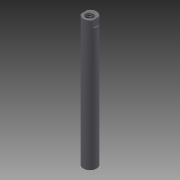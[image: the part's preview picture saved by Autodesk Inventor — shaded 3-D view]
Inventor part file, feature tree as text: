
AUTODESK INVENTOR PART (.ipt)
format: ipt  version: 2014 (Build 180170000, 170)  size: 134,656 bytes
history: native  units: in
note: dims shown in document units (in); Inventor stores cm internally (conversion verified against a paired STEP export)
features: other x84, sketch x3, revolve x1, hole x1, extrude x1
ambient origin geometry x8: Origin, YZ Plane, XZ Plane, XY Plane, X Axis, Y Axis, Z Axis, Center Point
bodies: Solid1 (feature_tree)
feature tree (90):
  revolve  "Revolution1"  [1 undecoded]
  hole  "Hole1"  [1 undecoded]
  extrude  "Extrusion1"  [1 undecoded]
  other  "b11_XY"
  other  "b11_YZ"
  other  "b11_ZX"
  other  "b11_X"
  other  "b11_Y"
  other  "b11_Z"
  other  "b11_Center"
  other  "b2_XY"
  other  "b2_YZ"
  other  "b2_ZX"
  other  "b2_X"
  other  "b2_Y"
  other  "b2_Z"
  other  "b2_Center"
  other  "e1_XY"
  other  "e1_YZ"
  other  "e1_ZX"
  other  "e1_X"
  other  "e1_Y"
  other  "e1_Z"
  other  "e1_Center"
  other  "e2_XY"
  other  "e2_YZ"
  other  "e2_ZX"
  other  "e2_X"
  other  "e2_Y"
  other  "e2_Z"
  other  "e2_Center"
  other  "f1_XY"
  other  "f1_YZ"
  other  "f1_ZX"
  other  "f1_X"
  other  "f1_Y"
  other  "f1_Z"
  other  "f1_Center"
  other  "f2_XY"
  other  "f2_YZ"
  other  "f2_ZX"
  other  "f2_X"
  other  "f2_Y"
  other  "f2_Z"
  other  "f2_Center"
  other  "h1_XY"
  other  "h1_YZ"
  other  "h1_ZX"
  other  "h1_X"
  other  "h1_Y"
  other  "h1_Z"
  other  "h1_Center"
  other  "h2_XY"
  other  "h2_YZ"
  other  "h2_ZX"
  other  "h2_X"
  other  "h2_Y"
  other  "h2_Z"
  other  "h2_Center"
  other  "rod_XY"
  other  "rod_YZ"
  other  "rod_ZX"
  other  "rod_X"
  other  "rod_Y"
  other  "rod_Z"
  other  "rod_Center"
  other  "rod_to_part_XY"
  other  "rod_to_part_YZ"
  other  "rod_to_part_ZX"
  other  "rod_to_part_X"
  other  "rod_to_part_Y"
  other  "rod_to_part_Z"
  other  "rod_to_part_Center"
  other  "to_rod_pivot_XY"
  other  "to_rod_pivot_YZ"
  other  "to_rod_pivot_ZX"
  other  "to_rod_pivot_X"
  other  "to_rod_pivot_Y"
  other  "to_rod_pivot_Z"
  other  "to_rod_pivot_Center"
  other  "to_rod_pivot1_XY"
  other  "to_rod_pivot1_YZ"
  other  "to_rod_pivot1_ZX"
  other  "to_rod_pivot1_X"
  other  "to_rod_pivot1_Y"
  other  "to_rod_pivot1_Z"
  other  "to_rod_pivot1_Center"
  sketch  "Sketch_1"  dims[d0=360.0deg]
  sketch  "Sketch2"  dims[d1=0.134in d2=0.46in d3=0.164in d4=0.25in d5=90.0deg d6=0.46in d7=0.0in d8=0.13in d9=0.0in]
  sketch  "Sketch_29"
note: 3 required parameter values undecoded (feature->parameter linkage not recoverable at this tier; creation-order binding heuristic only, values carry confidence <= 0.55)